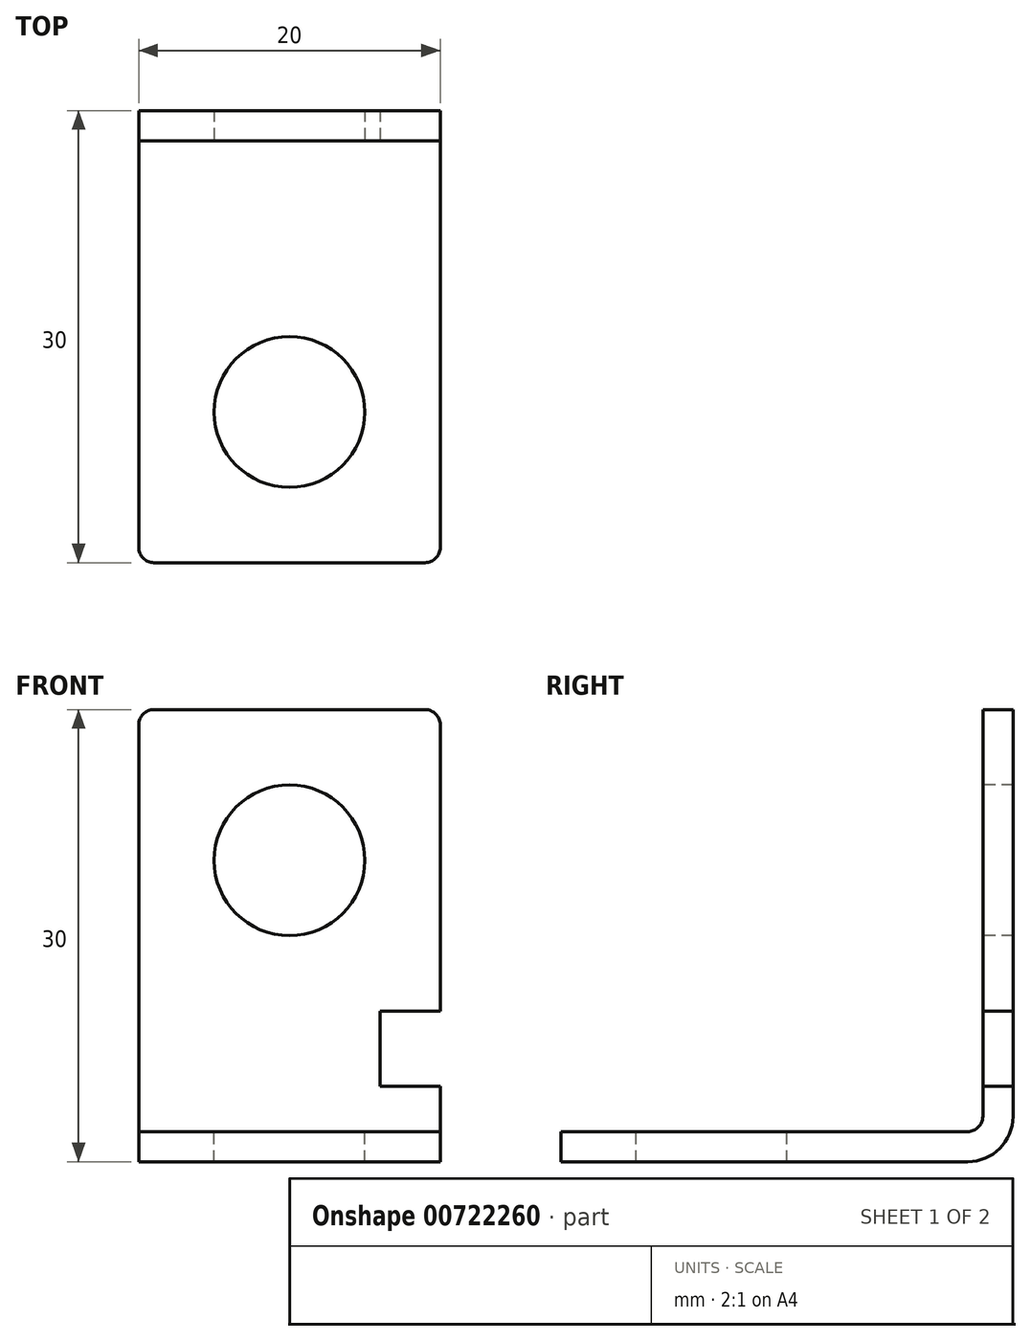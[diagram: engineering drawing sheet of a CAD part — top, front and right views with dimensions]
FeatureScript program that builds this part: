
annotation { "Feature Type Name" : "Feature", "Feature Type Description" : "" }
export const myFeature = defineFeature(function(context is Context, id is Id, definition is map)
    precondition{}
    {
        {
            var Q0;
            Q0=qCreatedBy(makeId("Right.planeOp"),FACE);
            var sketch = newSketch(context, id + "F0", { "sketchPlane" : qUnion([Q0])});
            skLineSegment(sketch, "E0", {"start": v(-26.85, 1) * mm, "end": v(3.15, 1) * mm});
            skLineSegment(sketch, "E1", {"start": v(3.15, 1) * mm, "end": v(3.15, 31) * mm});
            skLineSegment(sketch, "E2", {"start": v(3.15, 31) * mm, "end": v(1.15, 31) * mm});
            skLineSegment(sketch, "E3", {"start": v(1.15, 31) * mm, "end": v(1.15, 3) * mm});
            skLineSegment(sketch, "E4", {"start": v(1.15, 3) * mm, "end": v(-26.85, 3) * mm});
            skLineSegment(sketch, "E5", {"start": v(-26.85, 3) * mm, "end": v(-26.85, 1) * mm});
            skPoint(sketch, "E6", {"position": v(2.15, 31) * mm});
            skPoint(sketch, "E7", {"position": v(-26.85, 2) * mm});
            skSolve(sketch);
        }
        {
            var Q0;
            Q0=makeQuery(id+"F0.imprint","IMPRINT",FACE,{"disambiguationData":[TD([[makeQuery(id+"F0.imprint","IMPRINT",EDGE,{"derivedFrom":sQuery(id+"F0.wireOp",EDGE,"E0")}),1.0]])]});
            extrude(context, id + "F1", {"entities" : qUnion([Q0]), "endBound" : BoundingType.SYMMETRIC, "depth" : 20 * mm, "offsetDistance" : 25 * mm});
        }
        {
            var Q0;
            Q0=makeQuery(id+"F1.opExtrude","SWEPT_EDGE",EDGE,{"disambiguationData":[OSD([sQuery(id+"F0.wireOp",EDGE,"E3"),sQuery(id+"F0.wireOp",EDGE,"E4")])]});
            var Q1;
            Q1=makeQuery(id+"F1.opExtrude","CAP_EDGE",EDGE,{"disambiguationData":[OSD([sQuery(id+"F0.wireOp",EDGE,"E2")])],"isStart":false});
            var Q2;
            Q2=makeQuery(id+"F1.opExtrude","CAP_EDGE",EDGE,{"disambiguationData":[OSD([sQuery(id+"F0.wireOp",EDGE,"E2")])],"isStart":true});
            var Q3;
            Q3=makeQuery(id+"F1.opExtrude","CAP_EDGE",EDGE,{"disambiguationData":[OSD([sQuery(id+"F0.wireOp",EDGE,"E5")])],"isStart":false});
            var Q4;
            Q4=makeQuery(id+"F1.opExtrude","CAP_EDGE",EDGE,{"disambiguationData":[OSD([sQuery(id+"F0.wireOp",EDGE,"E5")])],"isStart":true});
            fillet(context, id + "F2", {"entities" : qUnion([Q0, Q1, Q2, Q3, Q4]), "radius" : 1 * mm, "tangentPropagation" : true, "allowEdgeOverflow" : false});
        }
        {
            var Q0;
            Q0=makeQuery(id+"F1.opExtrude","SWEPT_FACE",FACE,{"disambiguationData":[OSD([sQuery(id+"F0.wireOp",EDGE,"E4")])]});
            var sketch = newSketch(context, id + "F3", { "sketchPlane" : qUnion([Q0])});
            skCircle(sketch, "E8", {"center": v(0, -16.85) * mm, "radius": 5 * mm});
            skSolve(sketch);
        }
        {
            var Q0;
            Q0 = qSketchRegion(id + "F3", true);
            extrude(context, id + "F4", {"entities" : qUnion([Q0]), "operationType" : NewBodyOperationType.REMOVE, "oppositeDirection" : true, "depth" : 25 * mm, "offsetDistance" : 25 * mm});
        }
        {
            var Q0;
            Q0=makeQuery(id+"F1.opExtrude","SWEPT_FACE",FACE,{"disambiguationData":[OSD([sQuery(id+"F0.wireOp",EDGE,"E3")])]});
            var sketch = newSketch(context, id + "F5", { "sketchPlane" : qUnion([Q0])});
            skCircle(sketch, "E9", {"center": v(0, 21) * mm, "radius": 5 * mm});
            skSolve(sketch);
        }
        {
            var Q0;
            Q0=makeQuery(id+"F5.imprint","IMPRINT",FACE,{"disambiguationData":[TD([[makeQuery(id+"F5.imprint","IMPRINT",EDGE,{"derivedFrom":sQuery(id+"F5.wireOp",EDGE,"E9")}),1.0]])]});
            extrude(context, id + "F6", {"entities" : qUnion([Q0]), "operationType" : NewBodyOperationType.REMOVE, "oppositeDirection" : true, "depth" : 25 * mm, "offsetDistance" : 25 * mm});
        }
        {
            var Q0;
            Q0=makeQuery(id+"F1.opExtrude","SWEPT_FACE",FACE,{"disambiguationData":[OSD([sQuery(id+"F0.wireOp",EDGE,"E3")])]});
            var sketch = newSketch(context, id + "F7", { "sketchPlane" : qUnion([Q0])});
            skLineSegment(sketch, "E10.bottom", {"start": v(10, 11) * mm, "end": v(6, 11) * mm});
            skLineSegment(sketch, "E10.top", {"start": v(10, 6) * mm, "end": v(6, 6) * mm});
            skLineSegment(sketch, "E10.left", {"start": v(10, 11) * mm, "end": v(10, 6) * mm});
            skLineSegment(sketch, "E10.right", {"start": v(6, 11) * mm, "end": v(6, 6) * mm});
            skSolve(sketch);
        }
        {
            var Q0;
            Q0 = qSketchRegion(id + "F7", true);
            extrude(context, id + "F8", {"entities" : qUnion([Q0]), "operationType" : NewBodyOperationType.REMOVE, "oppositeDirection" : true, "depth" : 25 * mm, "offsetDistance" : 25 * mm});
        }
        {
            var Q0;
            Q0=makeQuery(id+"F1.opExtrude","SWEPT_EDGE",EDGE,{"disambiguationData":[OSD([sQuery(id+"F0.wireOp",EDGE,"E0"),sQuery(id+"F0.wireOp",EDGE,"E1")])]});
            fillet(context, id + "F9", {"entities" : qUnion([Q0]), "radius" : 3 * mm, "tangentPropagation" : true, "allowEdgeOverflow" : false});
        }
    });
